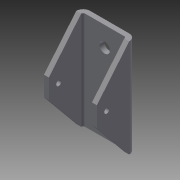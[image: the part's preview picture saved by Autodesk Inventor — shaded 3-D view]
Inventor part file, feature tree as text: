
AUTODESK INVENTOR PART (.ipt)
format: ipt  version: 2013 (Build 170138000, 138)  size: 131,584 bytes
history: native  units: in
note: dims shown in document units (in); Inventor stores cm internally (conversion verified against a paired STEP export)
features: sheet_metal_op x7, sketch x4, other x3, extrude x1
ambient origin geometry x8: Origin, YZ Plane, XZ Plane, XY Plane, X Axis, Y Axis, Z Axis, Center Point
bodies: Solid1 (feature_tree)
feature tree (15):
  sheet_metal_op  "Face1"
  sheet_metal_op  "Flange1"
  sketch  "Sketch3"  dims[d3=0.266in]
  sheet_metal_op  "Flange2"
  extrude  "Extrusion1"  Depth=2.5in
  sketch  "Sketch1"  dims[d0=1.0in d1=2.5in]
  other  "Plate1"
  sketch  "Sketch2"  dims[d2=0.266in]
  other  "Plate2"
  sheet_metal_op  "Bend1"
  sheet_metal_op  "Corner1"
  sketch  "Sketch4"  dims[d4=0.5in d5=0.5in d6=0.5in d7=0.5in d8=0.125in d9=0.125in d10=0.0625in d11=0.25in d12=0.125in d13=1.0in d14=90.0deg d15=0.05in d16=0.5in d17=0.125in d18=0.125in d19=0.125in d20=0.25in d21=1.25in d22=0.5in d23=1.0in d26=0.125in d27=0.0625in d28=0.25in d29=0.125in d30=1.0in d31=90.0deg d32=0.05in d33=0.5in d34=0.125in d35=0.125in d36=3.0in d37=0.0in]
  other  "Plate3"
  sheet_metal_op  "Bend2"
  sheet_metal_op  "Corner2"
